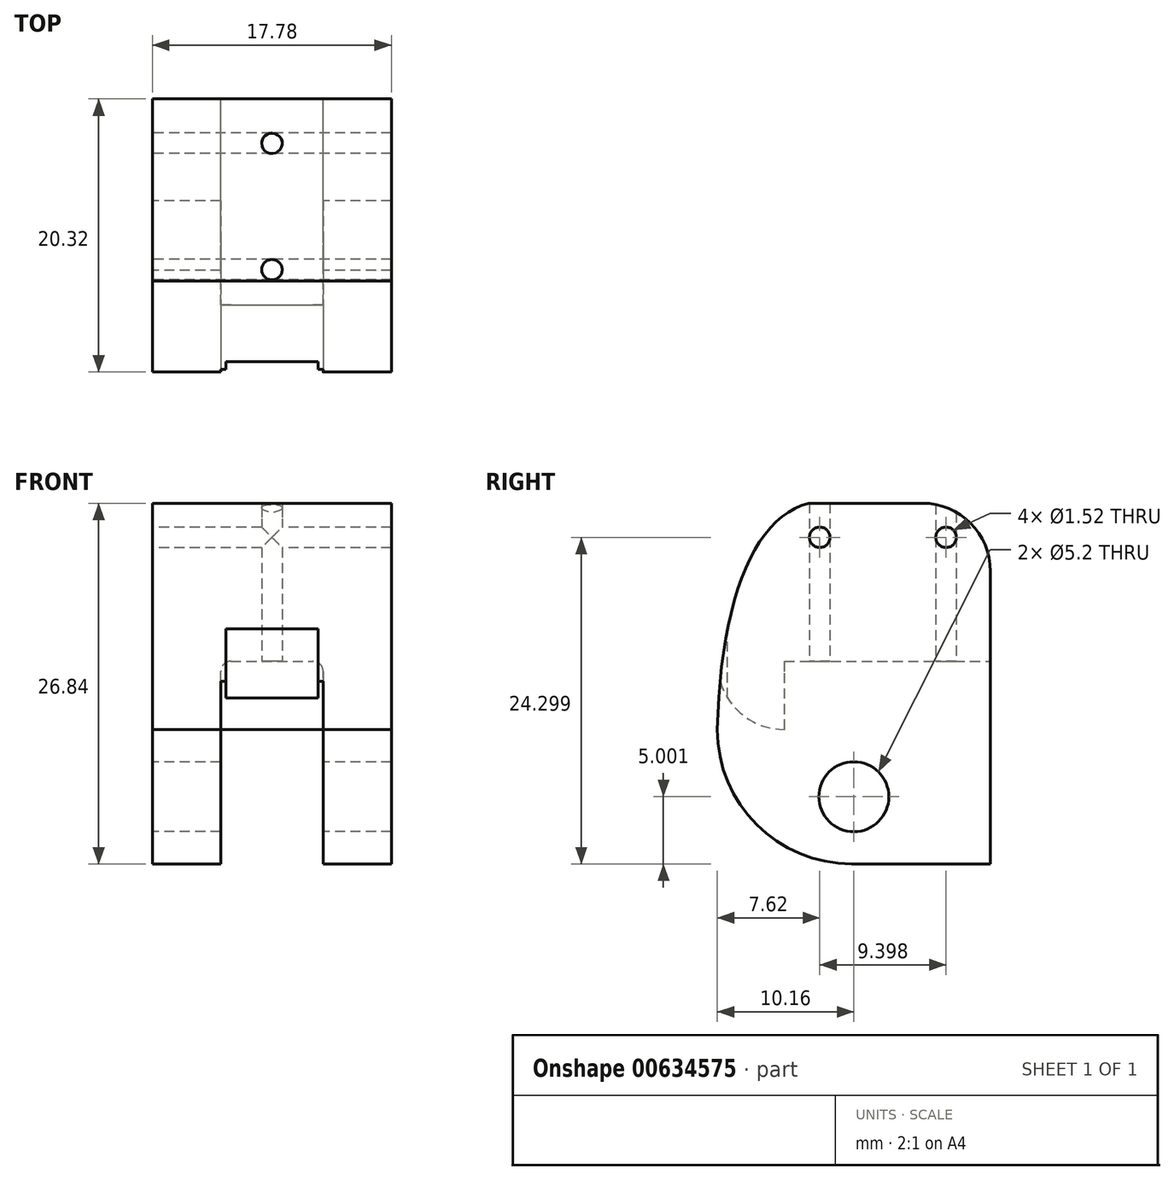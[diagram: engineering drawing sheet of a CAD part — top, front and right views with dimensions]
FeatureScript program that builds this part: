
annotation { "Feature Type Name" : "Feature", "Feature Type Description" : "" }
export const myFeature = defineFeature(function(context is Context, id is Id, definition is map)
    precondition{}
    {
        {
            var Q0;
            Q0=qCreatedBy(makeId("Front.planeOp"),FACE);
            var sketch = newSketch(context, id + "F0", { "sketchPlane" : qUnion([Q0])});
            skLineSegment(sketch, "E0.top", {"start": v(8.89, -13.42) * mm, "end": v(3.8, -13.42) * mm});
            skLineSegment(sketch, "E0.left", {"start": v(8.89, 13.42) * mm, "end": v(8.89, -13.42) * mm});
            skLineSegment(sketch, "E0.right", {"start": v(-8.9, 13.42) * mm, "end": v(-8.9, -13.42) * mm});
            skPoint(sketch, "E0.middle", {"position": v(0, 0) * mm});
            skLineSegment(sketch, "E1.left", {"start": v(3.8, -13.42) * mm, "end": v(3.8, -3.42) * mm});
            skLineSegment(sketch, "E2.trimOffspring", {"start": v(-3.81, -13.42) * mm, "end": v(-8.9, -13.42) * mm});
            skLineSegment(sketch, "E3", {"start": v(-8.9, 13.42) * mm, "end": v(8.89, 13.42) * mm});
            skLineSegment(sketch, "E4", {"start": v(-3.81, -13.42) * mm, "end": v(-3.81, -3.42) * mm});
            skLineSegment(sketch, "E5", {"start": v(-3.81, -3.42) * mm, "end": v(3.8, -3.42) * mm});
            skSolve(sketch);
        }
        {
            var Q0;
            Q0=makeQuery(id+"F0.imprint","IMPRINT",FACE,{"disambiguationData":[TD([[makeQuery(id+"F0.imprint","IMPRINT",EDGE,{"derivedFrom":sQuery(id+"F0.wireOp",EDGE,"E0.bottom")}),1.0]])]});
            var Q1;
            Q1=makeQuery(id+"F0.imprint","IMPRINT",FACE,{"disambiguationData":[TD([[makeQuery(id+"F0.imprint","IMPRINT",EDGE,{"derivedFrom":sQuery(id+"F0.wireOp",EDGE,"E0.top")}),-1.0]])]});
            extrude(context, id + "F1", {"entities" : qUnion([Q0, Q1]), "endBound" : BoundingType.SYMMETRIC, "depth" : 20.32 * mm, "offsetDistance" : 25.4 * mm});
        }
        {
            var Q0;
            Q0=makeQuery(id+"F1.opExtrude","SWEPT_FACE",FACE,{"disambiguationData":[OSD([sQuery(id+"F0.wireOp",EDGE,"E0.right")])]});
            var sketch = newSketch(context, id + "F2", { "sketchPlane" : qUnion([Q0])});
            skPoint(sketch, "E6.endSnap0", {"position": v(0, -13.42) * mm});
            skCircle(sketch, "E7", {"center": v(0, -8.42) * mm, "radius": 2.6 * mm});
            skSolve(sketch);
        }
        {
            var Q0;
            Q0=makeQuery(id+"F2.imprint","IMPRINT",FACE,{"disambiguationData":[TD([[makeQuery(id+"F2.imprint","IMPRINT",EDGE,{"derivedFrom":sQuery(id+"F2.wireOp",EDGE,"E7")}),1.0]])]});
            extrude(context, id + "F3", {"entities" : qUnion([Q0]), "operationType" : NewBodyOperationType.REMOVE, "endBound" : BoundingType.THROUGH_ALL, "oppositeDirection" : true, "depth" : 25.4 * mm, "offsetDistance" : 25.4 * mm});
        }
        {
            var Q0;
            Q0=makeQuery(id+"F1.opExtrude","CAP_EDGE",EDGE,{"disambiguationData":[OSD([sQuery(id+"F0.wireOp",EDGE,"E0.top")])],"isStart":false});
            var Q1;
            Q1=makeQuery(id+"F1.opExtrude","CAP_EDGE",EDGE,{"disambiguationData":[OSD([sQuery(id+"F0.wireOp",EDGE,"E2.trimOffspring")])],"isStart":false});
            fillet(context, id + "F4", {"entities" : qUnion([Q0, Q1]), "radius" : 10 * mm, "tangentPropagation" : true, "allowEdgeOverflow" : false});
        }
        {
            var Q0;
            Q0=makeQuery(id+"F1.opExtrude","CAP_EDGE",EDGE,{"disambiguationData":[OSD([sQuery(id+"F0.wireOp",EDGE,"n1KhcOkA-morR-dHWE-QHtQ-fdfn4GYgakT7"),sQuery(id+"F0.wireOp",EDGE,"so1H2Mnw-W18e-9x4z-PSc0-3TYgFntjAnIa")])],"isStart":false});
            var Q1;
            Q1=makeQuery(id+"F1.opExtrude","CAP_EDGE",EDGE,{"disambiguationData":[OSD([sQuery(id+"F0.wireOp",EDGE,"E5")])],"isStart":false});
            fillet(context, id + "F5", {"entities" : qUnion([Q0, Q1]), "radius" : 5 * mm, "tangentPropagation" : true, "allowEdgeOverflow" : false});
        }
        {
            var Q0;
            Q0=makeQuery(id+"F1.opExtrude","SWEPT_FACE",FACE,{"disambiguationData":[OSD([sQuery(id+"F0.wireOp",EDGE,"E0.right")])]});
            var sketch = newSketch(context, id + "F6", { "sketchPlane" : qUnion([Q0])});
            skLineSegment(sketch, "E8", {"start": v(10.16, 13.42) * mm, "end": v(10.16, -3.42) * mm});
            skEllipse(sketch, "E9", {"center": v(-7.08, -25.89) * mm, "majorRadius": 40.68 * mm, "minorRadius": 14.2 * mm, "majorAxis": v(0.26, 0.97)});
            skPoint(sketch, "E10", {"position": v(0, 13.42) * mm});
            skLineSegment(sketch, "E11", {"start": v(10.16, 13.42) * mm, "end": v(3.39, 13.42) * mm});
            skSolve(sketch);
        }
        {
            var Q0;
            {var subQ0=sQuery(id+"F6.wireOp",EDGE,"E8");Q0=makeQuery(id+"F6.imprint","IMPRINT",FACE,{"disambiguationData":[TD([[makeQuery(id+"F6.imprint","IMPRINT",EDGE,{"derivedFrom":subQ0}),-1.0]])]});}
            extrude(context, id + "F7", {"entities" : qUnion([Q0]), "operationType" : NewBodyOperationType.REMOVE, "endBound" : BoundingType.THROUGH_ALL, "oppositeDirection" : true, "depth" : 25.4 * mm, "offsetDistance" : 25.4 * mm});
        }
        {
            var Q0;
            Q0=makeQuery(id+"F1.opExtrude","CAP_EDGE",EDGE,{"disambiguationData":[OSD([sQuery(id+"F0.wireOp",EDGE,"E3")])],"isStart":true});
            fillet(context, id + "F8", {"entities" : qUnion([Q0]), "radius" : 5.08 * mm, "tangentPropagation" : true, "allowEdgeOverflow" : false});
        }
        {
            var Q0;
            Q0=makeQuery(id+"F1.opExtrude","SWEPT_FACE",FACE,{"disambiguationData":[OSD([sQuery(id+"F0.wireOp",EDGE,"E5")])]});
            var sketch = newSketch(context, id + "F9", { "sketchPlane" : qUnion([Q0])});
            skLineSegment(sketch, "E12", {"start": v(0, -10.16) * mm, "end": v(0, -7.62) * mm});
            skCircle(sketch, "E13", {"center": v(0, -6.86) * mm, "radius": 0.76 * mm});
            skCircle(sketch, "E14", {"center": v(0, 2.54) * mm, "radius": 0.76 * mm});
            skLineSegment(sketch, "E15", {"start": v(-8.9, 10.16) * mm, "end": v(8.89, 10.16) * mm});
            skLineSegment(sketch, "E16", {"start": v(0, 10.16) * mm, "end": v(0, 3.3) * mm});
            skSolve(sketch);
        }
        {
            var Q0;
            Q0=makeQuery(id+"F9.imprint","IMPRINT",FACE,{"disambiguationData":[TD([[makeQuery(id+"F9.imprint","IMPRINT",EDGE,{"derivedFrom":sQuery(id+"F9.wireOp",EDGE,"E14")}),1.0]])]});
            var Q1;
            Q1=makeQuery(id+"F9.imprint","IMPRINT",FACE,{"disambiguationData":[TD([[makeQuery(id+"F9.imprint","IMPRINT",EDGE,{"derivedFrom":sQuery(id+"F9.wireOp",EDGE,"E13")}),1.0]])]});
            extrude(context, id + "F10", {"entities" : qUnion([Q0, Q1]), "operationType" : NewBodyOperationType.REMOVE, "endBound" : BoundingType.THROUGH_ALL, "oppositeDirection" : true, "depth" : 25.4 * mm, "offsetDistance" : 25.4 * mm});
        }
        {
            var Q0;
            Q0=makeQuery(id+"F1.opExtrude","SWEPT_FACE",FACE,{"disambiguationData":[OSD([sQuery(id+"F0.wireOp",EDGE,"E0.right")])]});
            var sketch = newSketch(context, id + "F11", { "sketchPlane" : qUnion([Q0])});
            skLineSegment(sketch, "E17", {"start": v(-7.62, 13.42) * mm, "end": v(-7.62, 10.88) * mm});
            skLineSegment(sketch, "E18", {"start": v(-7.62, 10.88) * mm, "end": v(-10.16, 10.88) * mm});
            skLineSegment(sketch, "E19", {"start": v(10.16, 10.88) * mm, "end": v(3.3, 10.88) * mm});
            skLineSegment(sketch, "E20", {"start": v(3.3, 10.88) * mm, "end": v(3.3, 13.42) * mm});
            skCircle(sketch, "E21", {"center": v(-6.86, 10.88) * mm, "radius": 0.76 * mm});
            skCircle(sketch, "E22", {"center": v(2.54, 10.88) * mm, "radius": 0.76 * mm});
            skLineSegment(sketch, "E23", {"start": v(-10.16, -13.42) * mm, "end": v(10.16, -13.42) * mm});
            skLineSegment(sketch, "E24", {"start": v(10.16, -13.42) * mm, "end": v(10.16, 10.88) * mm});
            skSolve(sketch);
        }
        {
            var Q0;
            Q0=makeQuery(id+"F11.imprint","IMPRINT",FACE,{"disambiguationData":[TD([[makeQuery(id+"F11.imprint","IMPRINT",EDGE,{"derivedFrom":sQuery(id+"F11.wireOp",EDGE,"E21")}),1.0]])]});
            var Q1;
            Q1=makeQuery(id+"F11.imprint","IMPRINT",FACE,{"disambiguationData":[TD([[makeQuery(id+"F11.imprint","IMPRINT",EDGE,{"derivedFrom":sQuery(id+"F11.wireOp",EDGE,"E22")}),1.0]])]});
            extrude(context, id + "F12", {"entities" : qUnion([Q0, Q1]), "operationType" : NewBodyOperationType.REMOVE, "endBound" : BoundingType.THROUGH_ALL, "oppositeDirection" : true, "depth" : 25.4 * mm, "offsetDistance" : 25.4 * mm});
        }
        {
            var Q0;
            {var subQ0=sQuery(id+"F0.wireOp",EDGE,"E2.trimOffspring");var subQ1=sQuery(id+"F0.wireOp",EDGE,"E0.right");var subQ2=sQuery(id+"F0.wireOp",EDGE,"E0.top");Q0=makeQuery(id+"F7.boolean.opBoolean","MERGE",EDGE,{"derivedFrom":[makeQuery(id+"F4.opFillet","BLEND_EDGE",EDGE,{"blendedFrom":[makeQuery(id+"F1.opExtrude","CAP_EDGE",EDGE,{"disambiguationData":[OSD([subQ2])],"isStart":false}),makeQuery(id+"F1.opExtrude","CAP_FACE",FACE,{"disambiguationData":[OSD([subQ2,sQuery(id+"F0.wireOp",EDGE,"E0.left"),subQ1,sQuery(id+"F0.wireOp",EDGE,"E1.left"),subQ0,sQuery(id+"F0.wireOp",EDGE,"E3"),sQuery(id+"F0.wireOp",EDGE,"E4"),sQuery(id+"F0.wireOp",EDGE,"E5")])],"isStart":false})],"blendedInto":[makeQuery(id+"F1.opExtrude","CAP_FACE",FACE,{"disambiguationData":[OSD([subQ2,sQuery(id+"F0.wireOp",EDGE,"E0.left"),subQ1,sQuery(id+"F0.wireOp",EDGE,"E1.left"),subQ0,sQuery(id+"F0.wireOp",EDGE,"E3"),sQuery(id+"F0.wireOp",EDGE,"E4"),sQuery(id+"F0.wireOp",EDGE,"E5")])],"isStart":false})]}),makeQuery(id+"F7.opExtrude","SWEPT_EDGE",EDGE,{"disambiguationData":[OSD([subQ1,subQ0,sQuery(id+"F6.wireOp",EDGE,"E8"),sQuery(id+"F6.wireOp",EDGE,"E9")])]})]});}
            cPlane(context, id + "F13", {"entities" : qUnion([Q0]), "cplaneType" : CPlaneType.LINE_ANGLE, "offset" : 25.4 * mm, "angle" : 0 * degree, "width" : 152.4 * mm, "height" : 152.4 * mm});
        }
        {
            var Q0;
            Q0=qCreatedBy(id+"F13.planeOp",FACE);
            var sketch = newSketch(context, id + "F14", { "sketchPlane" : qUnion([Q0])});
            skLineSegment(sketch, "E25", {"start": v(-8.9, 13.42) * mm, "end": v(8.89, 13.42) * mm});
            skLineSegment(sketch, "E26", {"start": v(0, 13.42) * mm, "end": v(0, 10.37) * mm});
            skCircle(sketch, "E27", {"center": v(0, 6.94) * mm, "radius": 3.43 * mm});
            skLineSegment(sketch, "E28", {"start": v(-3.43, 6.94) * mm, "end": v(0, 6.94) * mm});
            skLineSegment(sketch, "E29", {"start": v(3.43, 6.94) * mm, "end": v(0, 6.94) * mm});
            skLineSegment(sketch, "E30", {"start": v(-3.43, 6.94) * mm, "end": v(-3.43, -3.42) * mm});
            skLineSegment(sketch, "E31", {"start": v(-3.43, -3.42) * mm, "end": v(3.43, -3.42) * mm});
            skLineSegment(sketch, "E32", {"start": v(3.43, -3.42) * mm, "end": v(3.43, 6.94) * mm});
            skSolve(sketch);
        }
        {
            var Q0;
            Q0=makeQuery(id+"F1.opExtrude","CAP_FACE",FACE,{"disambiguationData":[OSD([sQuery(id+"F0.wireOp",EDGE,"E0.top"),sQuery(id+"F0.wireOp",EDGE,"E0.left"),sQuery(id+"F0.wireOp",EDGE,"E0.right"),sQuery(id+"F0.wireOp",EDGE,"E1.left"),sQuery(id+"F0.wireOp",EDGE,"E2.trimOffspring"),sQuery(id+"F0.wireOp",EDGE,"E3"),sQuery(id+"F0.wireOp",EDGE,"E4"),sQuery(id+"F0.wireOp",EDGE,"E5")])],"isStart":true});
            var sketch = newSketch(context, id + "F15", { "sketchPlane" : qUnion([Q0])});
            skLineSegment(sketch, "E33.top", {"start": v(0, 1.66) * mm, "end": v(3.05, 1.66) * mm});
            skLineSegment(sketch, "E33.right", {"start": v(3.8, -3.42) * mm, "end": v(3.8, 0.9) * mm});
            skLineSegment(sketch, "E34.bottom", {"start": v(0, 1.66) * mm, "end": v(0, 1.66) * mm});
            skLineSegment(sketch, "E35.bottom", {"start": v(0, 1.66) * mm, "end": v(-3.05, 1.66) * mm});
            skLineSegment(sketch, "E35.right", {"start": v(-3.8, 0.9) * mm, "end": v(-3.8, -3.42) * mm});
            skArc(sketch, "E36.filletArc", {"start": v(3.8, 0.9) * mm, "mid": v(3.59, 1.44) * mm, "end": v(3.05, 1.66) * mm});
            skArc(sketch, "E37.filletArc", {"start": v(-3.05, 1.66) * mm, "mid": v(-3.59, 1.44) * mm, "end": v(-3.8, 0.9) * mm});
            skLineSegment(sketch, "E38", {"start": v(0, 1.66) * mm, "end": v(0, -3.42) * mm});
            skLineSegment(sketch, "E39", {"start": v(-3.8, -3.42) * mm, "end": v(3.81, -3.42) * mm});
            skSolve(sketch);
        }
        {
            var Q0;
            {var subQ5=sQuery(id+"F15.wireOp",EDGE,"E35.bottom");Q0=makeQuery(id+"F15.imprint","IMPRINT",FACE,{"disambiguationData":[TD([[makeQuery(id+"F15.imprint","IMPRINT",EDGE,{"derivedFrom":subQ5}),1.0]])]});}
            var Q1;
            {var subQ5=sQuery(id+"F15.wireOp",EDGE,"E33.top");Q1=makeQuery(id+"F15.imprint","IMPRINT",FACE,{"disambiguationData":[TD([[makeQuery(id+"F15.imprint","IMPRINT",EDGE,{"derivedFrom":subQ5}),-1.0]])]});}
            var Q2;
            {var subQ0=sQuery(id+"F0.wireOp",EDGE,"E5");Q2=makeQuery(id+"F5.opFillet","BLEND_VERTEX",VERTEX,{"blendedFrom":[makeQuery(id+"F1.opExtrude","CAP_EDGE",EDGE,{"disambiguationData":[OSD([subQ0])],"isStart":false}),makeQuery(id+"F1.opExtrude","SWEPT_FACE",FACE,{"disambiguationData":[OSD([subQ0])]}),makeQuery(id+"F1.opExtrude","SWEPT_FACE",FACE,{"disambiguationData":[OSD([sQuery(id+"F0.wireOp",EDGE,"E4")])]})],"blendedInto":[makeQuery(id+"F1.opExtrude","SWEPT_FACE",FACE,{"disambiguationData":[OSD([subQ0])]}),makeQuery(id+"F1.opExtrude","SWEPT_FACE",FACE,{"disambiguationData":[OSD([sQuery(id+"F0.wireOp",EDGE,"E4")])]})]});}
            extrude(context, id + "F16", {"entities" : qUnion([Q0, Q1]), "operationType" : NewBodyOperationType.REMOVE, "endBound" : BoundingType.UP_TO_VERTEX, "oppositeDirection" : true, "depth" : 13.97 * mm, "endBoundEntityVertex" : qUnion([Q2]), "offsetDistance" : 25.4 * mm});
        }
        {
            var Q0;
            {var subQ3=sQuery(id+"F14.wireOp",EDGE,"E28");Q0=makeQuery(id+"F14.imprint","IMPRINT",FACE,{"disambiguationData":[TD([[makeQuery(id+"F14.imprint","IMPRINT",EDGE,{"derivedFrom":subQ3}),1.0]])]});}
            var Q1;
            {var subQ0=sQuery(id+"F14.wireOp",EDGE,"E28");Q1=makeQuery(id+"F14.imprint","IMPRINT",FACE,{"disambiguationData":[TD([[makeQuery(id+"F14.imprint","IMPRINT",EDGE,{"derivedFrom":subQ0}),-1.0]])]});}
            var Q2;
            {var subQ0=sQuery(id+"F14.wireOp",EDGE,"E30");Q2=makeQuery(id+"F14.imprint","IMPRINT",FACE,{"disambiguationData":[TD([[makeQuery(id+"F14.imprint","IMPRINT",EDGE,{"derivedFrom":subQ0}),1.0]])]});}
            extrude(context, id + "F17", {"entities" : qUnion([Q0, Q1, Q2]), "operationType" : NewBodyOperationType.REMOVE, "oppositeDirection" : true, "depth" : 0.76 * mm, "offsetDistance" : 25.4 * mm});
        }
    });
